# Revit family: TY4153
name_source: partatom
category: Sprinklers
revit_build: Autodesk Revit 2016 (Build: 20150220_1215(x64)
units: mm (PartAtom-declared; Revit-internal decimal feet)

## family parameters
Always vertical = Yes
Cut with Voids When Loaded = No
Maintain Annotation Orientation = No
OmniClass Number = 23.65.70.17.11.24
OmniClass Title = Fire Fighting Sprinkler Heads
Part Type = Normal
Room Calculation Point = No
Round Connector Dimension = Use Diameter
Shared = No
Work Plane-Based = No

## types (12) — shared parameters
COBie = Yes
COBie.Component.Name = Sprinklers:Interm.Level Upr._SIN
COBie.Type = Yes
COBie.Type.AssetType = Fixed
COBie.Type.Category = Pr_70_55_97_84:Sprinklers
COBie.Type.DurationUnit = year
COBie.Type.Manufacturer = Tyco Fire Protection Products
COBie.Type.Material = Bronze
COBie.Type.Shape = Cylinder
COBie.Type.Size = 3/4"(DN20)
COBie.Type.WarrantyGuarantorParts = http://tycofsbp.com
Coverage = Standard
K-Factor = 114.87
Manufacturer = Tyco Fire Protection Products
Manufacturer URL = www.tyco-fire.com
Model = TY-B
Nominal Diameter 1 = 20 mm
Orifice = Extra Large
Orifice Size = 13 mm
Outside Diameter 1 = 27 mm
Response = Standard
SIN No = TY4153
Takeout 1 = 62 mm
Technical Data Sheet No = TFP351
zero-valued in all types: COBie.Type.NominalHeight, COBie.Type.NominalLength, COBie.Type.NominalWidth, COBie.Type.ReplacementCost, Style Id

## per-type parameters (varying)
| type | COBie.Component.Description | COBie.Type.Colour | COBie.Type.Finish | COBie.Type.ModelNumber | COBie.Type.ModelReference | Part No | Temperature Rating |
| TY-B Intermediate Level Upright Brass 135°F/57°C 8K ¾" NPT_57-543-1-135 | TY-B Wet Interm.Level Upr.  57.2°C K115 DN20 NPT Br | Yellow | Natural Brass | 57-543-1-135 | TY-B Wet Interm.Level Upr.  57.2°C K115 DN20 NPT Br | 57-543-1-135 | 57 °C |
| TY-B Intermediate Level Upright Brass 155°F/68°C 8K ¾" NPT_57-543-1-155 | TY-B Wet Interm.Level Upr.  68.3°C K115 DN20 NPT Br | Yellow | Natural Brass | 57-543-1-155 | TY-B Wet Interm.Level Upr.  68.3°C K115 DN20 NPT Br | 57-543-1-155 | 68 °C |
| TY-B Intermediate Level Upright Brass 175°F/79°C 8K ¾" NPT_57-543-1-175 | TY-B Wet Interm.Level Upr.  79.4°C K115 DN20 NPT Br | Yellow | Natural Brass | 57-543-1-175 | TY-B Wet Interm.Level Upr.  79.4°C K115 DN20 NPT Br | 57-543-1-175 | 79 °C |
| TY-B Intermediate Level Upright Brass 200°F/93°C 8K ¾" NPT_57-543-1-200 | TY-B Wet Interm.Level Upr.  93.3°C K115 DN20 NPT Br | Yellow | Natural Brass | 57-543-1-200 | TY-B Wet Interm.Level Upr.  93.3°C K115 DN20 NPT Br | 57-543-1-200 | 93 °C |
| TY-B Intermediate Level Upright Brass 286°F/141°C 8K ¾" NPT_57-543-1-286 | TY-B Wet Interm.Level Upr.  141.1°C K115 DN20 NPT Br | Yellow | Natural Brass | 57-543-1-286 | TY-B Wet Interm.Level Upr.  141.1°C K115 DN20 NPT Br | 57-543-1-286 | 141 °C |
| TY-B Intermediate Level Upright Brass 360°F/182°C 8K ¾" NPT_57-543-1-360 | TY-B Wet Interm.Level Upr.  182.2°C K115 DN20 NPT Br | Yellow | Natural Brass | 57-543-1-360 | TY-B Wet Interm.Level Upr.  182.2°C K115 DN20 NPT Br | 57-543-1-360 | 182 °C |
| TY-B Intermediate Level Upright Lead 135°F/57°C 8K ¾" NPT_57-543-7-135 | TY-B Wet Interm.Level Upr.  57.2°C K115 DN20 NPT Lead | Gray | Lead Coated | 57-543-7-135 | TY-B Wet Interm.Level Upr.  57.2°C K115 DN20 NPT Lead | 57-543-7-135 | 57 °C |
| TY-B Intermediate Level Upright Lead 155°F/68°C 8K ¾" NPT_57-543-7-155 | TY-B Wet Interm.Level Upr.  68.3°C K115 DN20 NPT Lead | Gray | Lead Coated | 57-543-7-155 | TY-B Wet Interm.Level Upr.  68.3°C K115 DN20 NPT Lead | 57-543-7-155 | 68 °C |
| TY-B Intermediate Level Upright Lead 175°F/79°C 8K ¾" NPT_57-543-7-175 | TY-B Wet Interm.Level Upr.  79.4°C K115 DN20 NPT Lead | Gray | Lead Coated | 57-543-7-175 | TY-B Wet Interm.Level Upr.  79.4°C K115 DN20 NPT Lead | 57-543-7-175 | 79 °C |
| TY-B Intermediate Level Upright Lead 200°F/93°C 8K ¾" NPT_57-543-7-200 | TY-B Wet Interm.Level Upr.  93.3°C K115 DN20 NPT Lead | Gray | Lead Coated | 57-543-7-200 | TY-B Wet Interm.Level Upr.  93.3°C K115 DN20 NPT Lead | 57-543-7-200 | 93 °C |
| TY-B Intermediate Level Upright Lead 286°F/141°C 8K ¾" NPT_57-543-7-286 | TY-B Wet Interm.Level Upr.  141.1°C K115 DN20 NPT Lead | Gray | Lead Coated | 57-543-7-286 | TY-B Wet Interm.Level Upr.  141.1°C K115 DN20 NPT Lead | 57-543-7-286 | 141 °C |
| TY-B Intermediate Level Upright Lead 360°F/182°C 8K ¾" NPT_57-543-7-360 | TY-B Wet Interm.Level Upr.  182.2°C K115 DN20 NPT Lead | Gray | Lead Coated | 57-543-7-360 | TY-B Wet Interm.Level Upr.  182.2°C K115 DN20 NPT Lead | 57-543-7-360 | 182 °C |

note: column(s) folded — value = type name in every type: Description

## geometry (parser evidence)
native form markers: Blend x2, Sweep x70
no freeform markers — native parametric forms only
